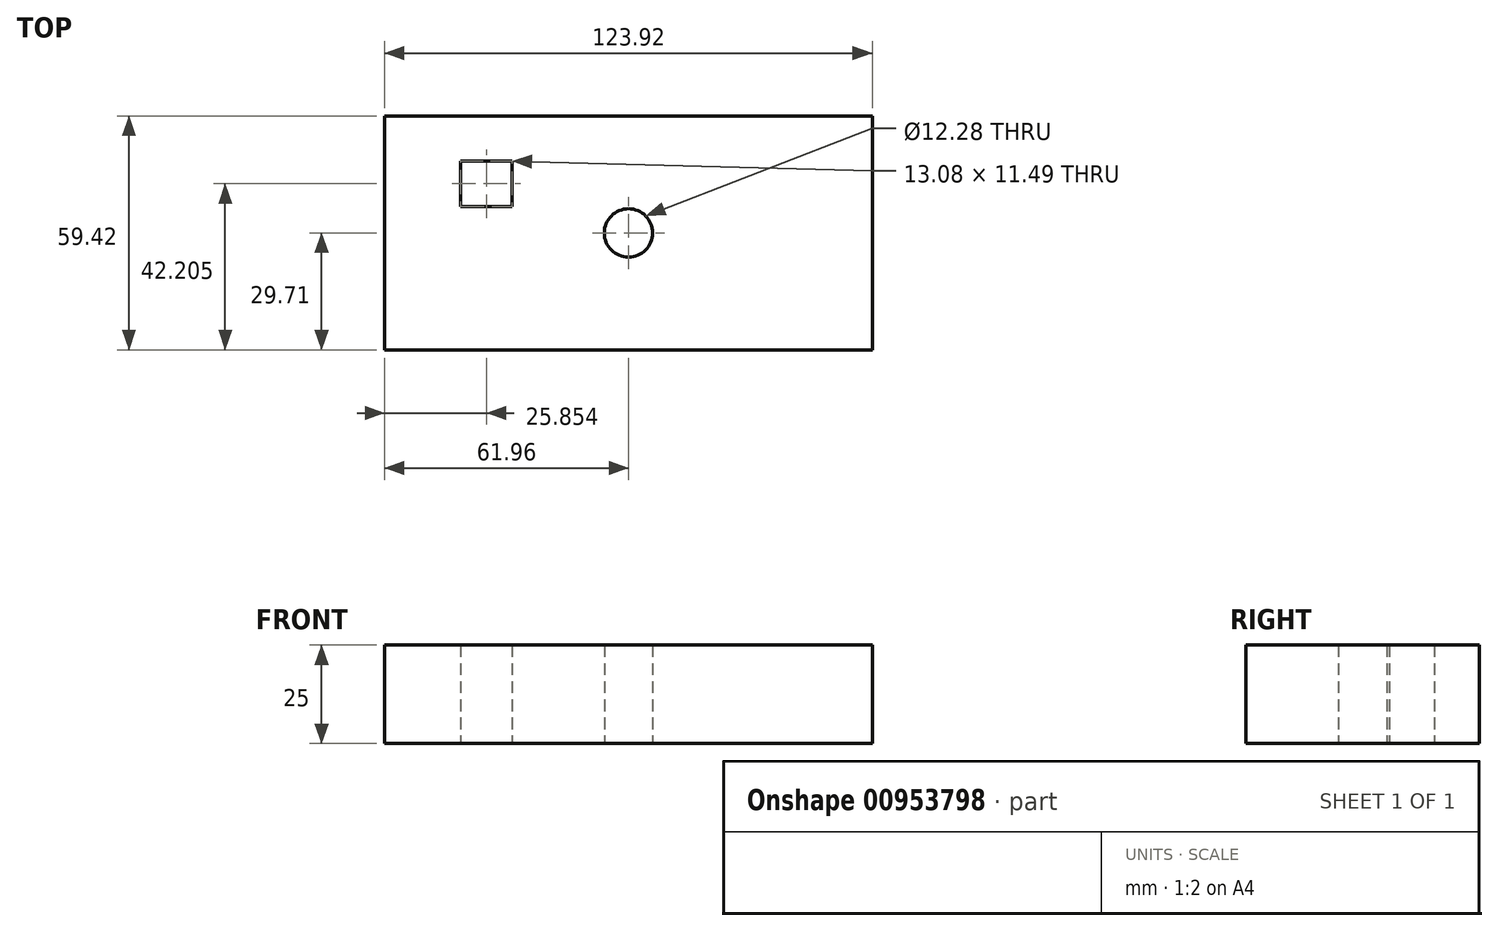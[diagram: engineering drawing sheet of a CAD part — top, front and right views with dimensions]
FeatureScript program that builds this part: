
annotation { "Feature Type Name" : "Feature", "Feature Type Description" : "" }
export const myFeature = defineFeature(function(context is Context, id is Id, definition is map)
    precondition{}
    {
        {
            var Q0;
            Q0=qCreatedBy(makeId("Top.planeOp"),FACE);
            var sketch = newSketch(context, id + "F0", { "sketchPlane" : qUnion([Q0])});
            skLineSegment(sketch, "E0.bottom", {"start": v(61.96, -29.7) * mm, "end": v(-61.96, -29.7) * mm});
            skLineSegment(sketch, "E0.top", {"start": v(61.96, 29.7) * mm, "end": v(-61.96, 29.7) * mm});
            skLineSegment(sketch, "E0.left", {"start": v(61.96, -29.7) * mm, "end": v(61.96, 29.7) * mm});
            skLineSegment(sketch, "E0.right", {"start": v(-61.96, -29.7) * mm, "end": v(-61.96, 29.7) * mm});
            skPoint(sketch, "E0.middle", {"position": v(0, 0) * mm});
            skCircle(sketch, "E1", {"center": v(0, 0) * mm, "radius": 6.14 * mm});
            skLineSegment(sketch, "E2.bottom", {"start": v(-42.64, 18.24) * mm, "end": v(-29.57, 18.24) * mm});
            skLineSegment(sketch, "E2.top", {"start": v(-42.64, 6.75) * mm, "end": v(-29.57, 6.75) * mm});
            skLineSegment(sketch, "E2.left", {"start": v(-42.64, 18.24) * mm, "end": v(-42.64, 6.75) * mm});
            skLineSegment(sketch, "E2.right", {"start": v(-29.57, 18.24) * mm, "end": v(-29.57, 6.75) * mm});
            skPoint(sketch, "E3.oppositeSnap0", {"position": v(-29.57, 12.5) * mm});
            skLineSegment(sketch, "E3.bottom", {"start": v(-29.57, 12.5) * mm, "end": v(-21.65, 12.5) * mm});
            skLineSegment(sketch, "E3.top", {"start": v(-29.57, 12.5) * mm, "end": v(-21.65, 12.5) * mm});
            skLineSegment(sketch, "E3.left", {"start": v(-29.57, 12.5) * mm, "end": v(-29.57, 12.5) * mm});
            skLineSegment(sketch, "E3.right", {"start": v(-21.65, 12.5) * mm, "end": v(-21.65, 12.5) * mm});
            skSolve(sketch);
        }
        {
            var Q0;
            Q0=makeQuery(id+"F0.imprint","IMPRINT",FACE,{"disambiguationData":[TD([[makeQuery(id+"F0.imprint","IMPRINT",EDGE,{"derivedFrom":sQuery(id+"F0.wireOp",EDGE,"E0.bottom")}),-1.0]])]});
            extrude(context, id + "F1", {"entities" : qUnion([Q0]), "depth" : 25 * mm, "offsetDistance" : 25 * mm});
        }
    });
